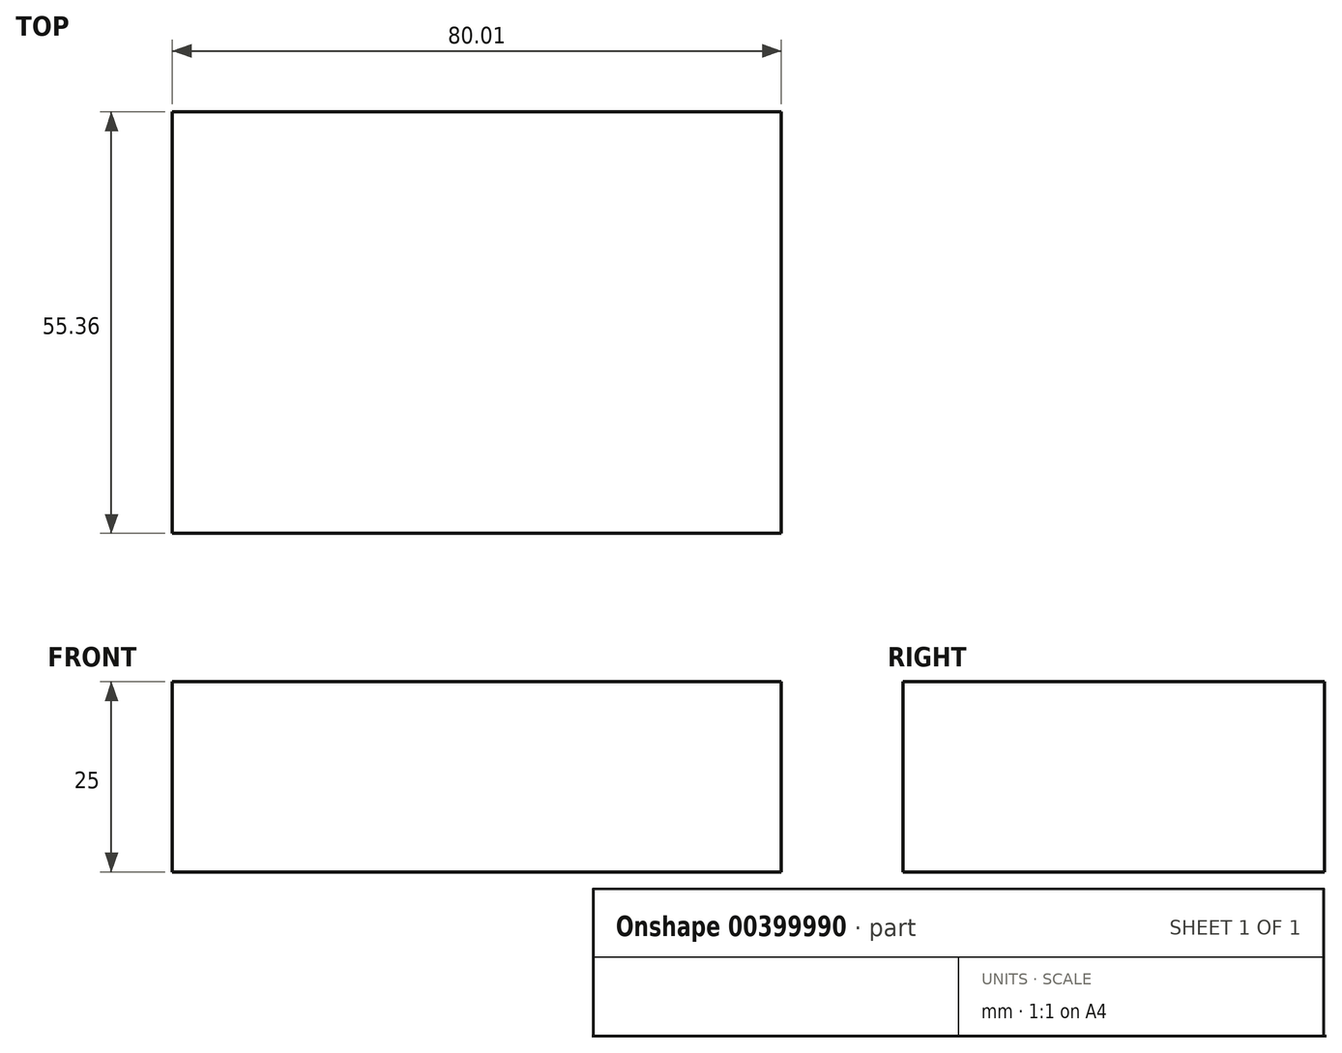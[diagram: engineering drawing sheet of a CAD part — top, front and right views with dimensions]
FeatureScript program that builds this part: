
annotation { "Feature Type Name" : "Feature", "Feature Type Description" : "" }
export const myFeature = defineFeature(function(context is Context, id is Id, definition is map)
    precondition{}
    {
        {
            var Q0;
            Q0=qCreatedBy(makeId("Top.planeOp"),FACE);
            var sketch = newSketch(context, id + "F0", { "sketchPlane" : qUnion([Q0])});
            skLineSegment(sketch, "E0.bottom", {"start": v(-53.98, -37.72) * mm, "end": v(26.03, -37.72) * mm});
            skLineSegment(sketch, "E0.top", {"start": v(-53.98, -93.08) * mm, "end": v(26.03, -93.08) * mm});
            skLineSegment(sketch, "E0.left", {"start": v(-53.98, -37.72) * mm, "end": v(-53.98, -93.08) * mm});
            skLineSegment(sketch, "E0.right", {"start": v(26.03, -37.72) * mm, "end": v(26.03, -93.08) * mm});
            skSolve(sketch);
        }
        {
            var Q0;
            Q0 = qSketchRegion(id + "F0", true);
            extrude(context, id + "F1", {"entities" : qUnion([Q0]), "depth" : 25 * mm});
        }
    });
